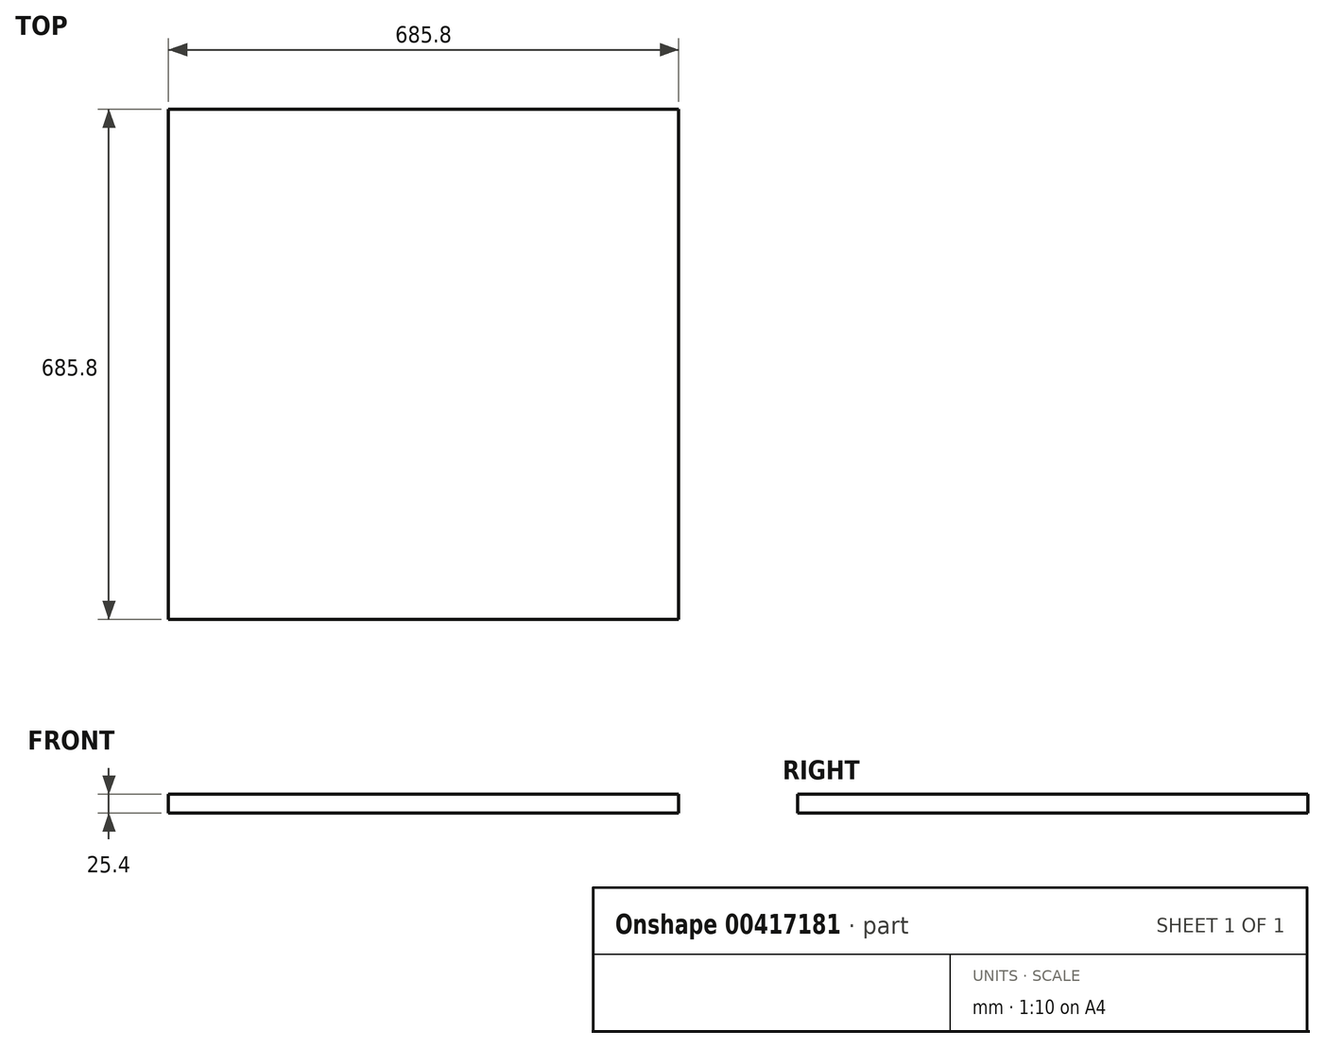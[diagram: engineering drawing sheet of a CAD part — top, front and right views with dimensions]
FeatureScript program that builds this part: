
annotation { "Feature Type Name" : "Feature", "Feature Type Description" : "" }
export const myFeature = defineFeature(function(context is Context, id is Id, definition is map)
    precondition{}
    {
        {
            var Q0;
            Q0=qCreatedBy(makeId("Top.planeOp"),FACE);
            var sketch = newSketch(context, id + "F0", { "sketchPlane" : qUnion([Q0])});
            skLineSegment(sketch, "E0.bottom", {"start": v(0, 0) * mm, "end": v(685.8, 0) * mm});
            skLineSegment(sketch, "E0.top", {"start": v(0, 685.8) * mm, "end": v(685.8, 685.8) * mm});
            skLineSegment(sketch, "E0.left", {"start": v(0, 0) * mm, "end": v(0, 685.8) * mm});
            skLineSegment(sketch, "E0.right", {"start": v(685.8, 0) * mm, "end": v(685.8, 685.8) * mm});
            skSolve(sketch);
        }
        {
            var Q0;
            Q0=makeQuery(id+"F0.imprint","IMPRINT",FACE,{"disambiguationData":[TD([[makeQuery(id+"F0.imprint","IMPRINT",EDGE,{"derivedFrom":sQuery(id+"F0.wireOp",EDGE,"E0.bottom")}),1.0]])]});
            extrude(context, id + "F1", {"entities" : qUnion([Q0]), "oppositeDirection" : true, "depth" : 25.4 * mm});
        }
    });
